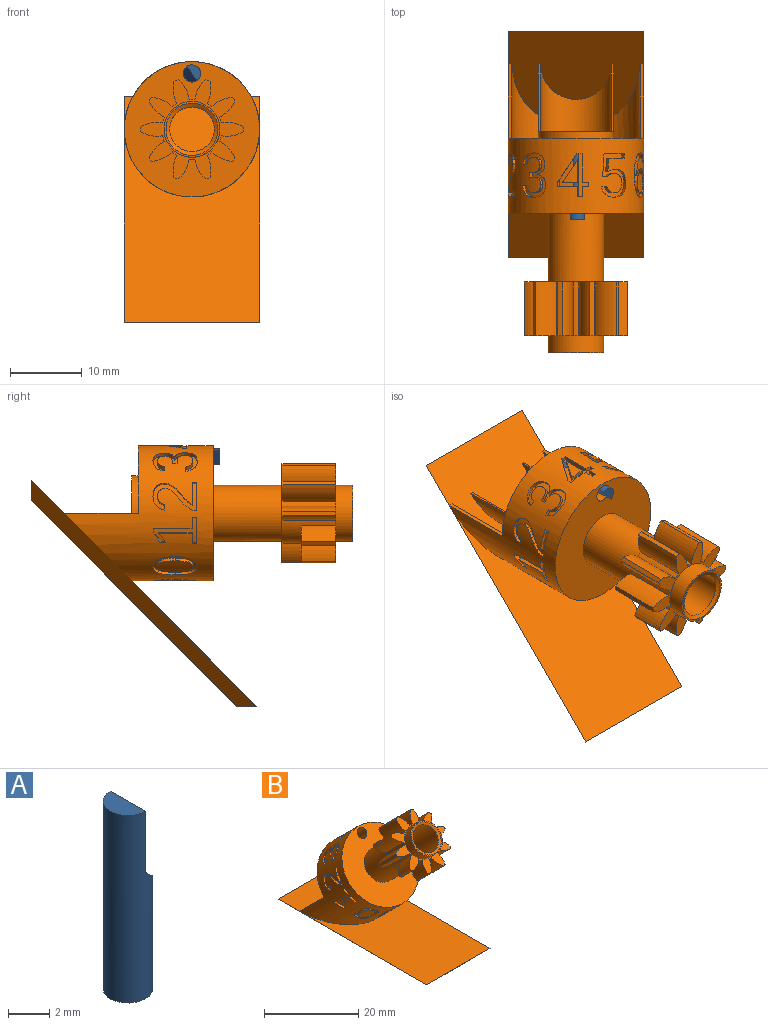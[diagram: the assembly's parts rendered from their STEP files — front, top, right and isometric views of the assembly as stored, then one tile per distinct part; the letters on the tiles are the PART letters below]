
ASSEMBLY  parts=2 mates=1
PART A: 5 faces, bbox 2.4x2.4x11.1 mm
  f0: cylinder r=1.2mm len=11.1mm, axis (0,0,-1), area 67.2mm2, adj f1,f2,f3,f4
  f1: plane 2.4x1.2mm, normal (0,0,1), area 2.3mm2, adj f0,f3
  f2: plane 2.4x2.4mm, normal (0,0,-1), area 4.5mm2, adj f0
  f3: plane 3.6x2.4mm, normal (1,0,0), area 8.6mm2, adj f0,f1,f4
  f4: plane 2.4x1.2mm, normal (0.71,0,0.71), area 3.2mm2, adj f0,f3
PART B: 299 faces, bbox 19.1x44.8x38.5 mm
  f0: cylinder r=9.45mm len=28.12mm, axis (0,0.71,-0.71), area 620.5mm2, adj f2,f4,f53,f54,f62,f63,f64,f65
  f1: cylinder r=5.25mm len=14.76mm, axis (0,0.71,-0.71), area 130.8mm2, adj f5,f6,f8,f53,f293
  f2: plane 7.34x7.34mm, normal (0,0.71,0.71), area 5.2mm2, adj f0,f3,f53,f293
  f3: cylinder r=8.95mm len=17.9mm, axis (0,-0.71,0.71), area 131.5mm2, adj f2,f4,f53,f293
  f4: plane 7.34x7.34mm, normal (0,0.71,0.71), area 5.2mm2, adj f0,f3,f53,f293
  f5: plane 6.7x6.7mm, normal (0,0.71,0.71), area 2.8mm2, adj f1,f7,f8,f293
  f6: plane 6.7x6.7mm, normal (0,0.71,0.71), area 2.8mm2, adj f1,f7,f8,f293
  f7: cylinder r=4.95mm len=10.2mm, axis (0,-0.71,0.71), area 98.3mm2, adj f5,f6,f8,f293
  f8: plane 10.5x7.21mm, normal (0,0.71,-0.71), area 26.4mm2, adj f1,f5,f6,f7,f52
  f9: plane 14.4x9.81mm, normal (0,0.71,-0.71), area 46.7mm2, adj f10,f11,f12,f19,f20,f21,f22,f23
  f10: cylinder r=4.5mm len=5.77mm, axis (0,0.71,-0.71), area 24.1mm2, adj f9,f11,f47,f48
  f11: cylinder r=7.2mm len=5.75mm, axis (0,0.71,-0.71), area 4.8mm2, adj f9,f10,f12,f48
  f12: cylinder r=4.5mm len=5.77mm, axis (0,0.71,-0.71), area 24.1mm2, adj f9,f11,f19,f48
  f13: cylinder r=4.5mm len=5.02mm, axis (0,0.71,-0.71), area 15.4mm2, adj f14,f19,f48,f50
  f14: cylinder r=7.2mm len=3.76mm, axis (0,0.71,-0.71), area 3.1mm2, adj f13,f15,f48,f50
  f15: cylinder r=4.5mm len=4.34mm, axis (0,0.71,-0.71), area 15.4mm2, adj f14,f19,f48,f50
  f16: cylinder r=4.5mm len=5.6mm, axis (0,0.71,-0.71), area 15.4mm2, adj f17,f19,f48,f49
  f17: cylinder r=7.2mm len=3.53mm, axis (0,0.71,-0.71), area 3.1mm2, adj f16,f18,f48,f49
  f18: cylinder r=4.5mm len=5.34mm, axis (0,0.71,-0.71), area 15.4mm2, adj f17,f19,f48,f49
  f19: cylinder r=4.2mm len=7.63mm, axis (0,0.71,-0.71), area 28mm2, adj f9,f12,f13,f15,f16,f18,f20,f48
  f20: cylinder r=4.5mm len=7.25mm, axis (0,0.71,-0.71), area 24.1mm2, adj f9,f19,f21,f48
  f21: cylinder r=7.2mm len=5.44mm, axis (0,0.71,-0.71), area 4.8mm2, adj f9,f20,f22,f48
  f22: cylinder r=4.5mm len=7.51mm, axis (0,0.71,-0.71), area 24.1mm2, adj f9,f21,f23,f48
  f23: cylinder r=4.2mm len=5.64mm, axis (0,0.71,-0.71), area 6mm2, adj f9,f22,f24,f48
  f24: cylinder r=4.5mm len=6.25mm, axis (0,0.71,-0.71), area 24.1mm2, adj f9,f23,f25,f48
  f25: cylinder r=7.2mm len=5.67mm, axis (0,0.71,-0.71), area 4.8mm2, adj f9,f24,f26,f48
  f26: cylinder r=4.5mm len=6.93mm, axis (0,0.71,-0.71), area 24.1mm2, adj f9,f25,f27,f48
  f27: cylinder r=4.2mm len=5.84mm, axis (0,0.71,-0.71), area 6mm2, adj f9,f26,f28,f48
  f28: cylinder r=4.5mm len=5.77mm, axis (0,0.71,-0.71), area 24.1mm2, adj f9,f27,f29,f48
  f29: cylinder r=7.2mm len=5.75mm, axis (0,0.71,-0.71), area 4.8mm2, adj f9,f28,f30,f48
  f30: cylinder r=4.5mm len=5.77mm, axis (0,0.71,-0.71), area 24.1mm2, adj f9,f29,f31,f48
  f31: cylinder r=4.2mm len=5.84mm, axis (0,0.71,-0.71), area 6mm2, adj f9,f30,f32,f48
  f32: cylinder r=4.5mm len=6.93mm, axis (0,0.71,-0.71), area 24.1mm2, adj f9,f31,f33,f48
  f33: cylinder r=7.2mm len=5.67mm, axis (0,0.71,-0.71), area 4.8mm2, adj f9,f32,f34,f48
  f34: cylinder r=4.5mm len=6.25mm, axis (0,0.71,-0.71), area 24.1mm2, adj f9,f33,f35,f48
  f35: cylinder r=4.2mm len=5.64mm, axis (0,0.71,-0.71), area 6mm2, adj f9,f34,f36,f48
  f36: cylinder r=4.5mm len=7.51mm, axis (0,0.71,-0.71), area 24.1mm2, adj f9,f35,f37,f48
  f37: cylinder r=7.2mm len=5.44mm, axis (0,0.71,-0.71), area 4.8mm2, adj f9,f36,f38,f48
  f38: cylinder r=4.5mm len=7.25mm, axis (0,0.71,-0.71), area 24.1mm2, adj f9,f37,f39,f48
  f39: cylinder r=4.2mm len=5.32mm, axis (0,0.71,-0.71), area 6mm2, adj f9,f38,f40,f48
  f40: cylinder r=4.5mm len=7.25mm, axis (0,0.71,-0.71), area 24.1mm2, adj f9,f39,f41,f48
  f41: cylinder r=7.2mm len=5.44mm, axis (0,0.71,-0.71), area 4.8mm2, adj f9,f40,f42,f48
  f42: cylinder r=4.5mm len=7.51mm, axis (0,0.71,-0.71), area 24.1mm2, adj f9,f41,f43,f48
  f43: cylinder r=4.2mm len=5.64mm, axis (0,0.71,-0.71), area 6mm2, adj f9,f42,f44,f48
  f44: cylinder r=4.5mm len=6.25mm, axis (0,0.71,-0.71), area 24.1mm2, adj f9,f43,f45,f48
  f45: cylinder r=7.2mm len=5.67mm, axis (0,0.71,-0.71), area 4.8mm2, adj f9,f44,f46,f48
  f46: cylinder r=4.5mm len=6.93mm, axis (0,0.71,-0.71), area 24.1mm2, adj f9,f45,f47,f48
  f47: cylinder r=4.2mm len=5.84mm, axis (0,0.71,-0.71), area 6mm2, adj f9,f10,f46,f48
  f48: plane 14.4x9.81mm, normal (0,-0.71,0.71), area 56.4mm2, adj f10,f11,f12,f13,f14,f15,f16,f17
  f49: plane 2.35x2.35mm, normal (0,0.71,-0.71), area 4.9mm2, adj f16,f17,f18,f19
  f50: plane 3.22x1.99mm, normal (0,0.71,-0.71), area 4.9mm2, adj f13,f14,f15,f19
  f51: cylinder r=3.9mm len=12.3mm, axis (0,0.71,-0.71), area 235.2mm2, adj f9,f54
  f52: cone r=3.12mm half-angle=30deg, axis (0,0.71,-0.71), area 49.7mm2, adj f8,f57
  f53: plane 18.9x13.01mm, normal (0,0.71,-0.71), area 175mm2, adj f0,f1,f2,f3,f4,f58
  f54: plane 18.9x13.36mm, normal (0,-0.71,0.71), area 228.2mm2, adj f0,f51,f58
  f55: cylinder r=3.9mm len=7.8mm, axis (0,0.71,-0.71), area 58.8mm2, adj f48,f56
  f56: plane 7.8x5.52mm, normal (0,-0.71,0.71), area 6.2mm2, adj f55,f59
  f57: cylinder r=3.12mm len=24.73mm, axis (0,0.71,-0.71), area 563.2mm2, adj f52,f59
  f58: cylinder r=1.2mm len=9.12mm, axis (0,-0.71,0.71), area 77.2mm2, adj f53,f54,f60,f61,f62,f63,f64,f65
  f59: cone r=3.64mm half-angle=60deg, axis (0,-0.71,0.71), area 12.7mm2, adj f56,f57
  f60: cylinder r=8.95mm len=4.38mm, axis (0,0.71,-0.71), area 4mm2, adj f58,f62,f66,f73,f74,f75,f76,f77
  f61: cylinder r=8.95mm len=2.98mm, axis (0,0.71,-0.71), area 3.2mm2, adj f58,f64,f65,f67,f71,f72,f79,f80
  f62: plane 0.74x0.39mm, normal (0,0.71,-0.71), area 0.4mm2, adj f0,f58,f60,f63,f75
  f63: plane 1.29x1.29mm, normal (1,0.02,0.02), area 0.6mm2, adj f0,f58,f62,f64
  f64: plane 2.84x0.57mm, normal (0,0.71,-0.71), area 1.4mm2, adj f0,f58,f61,f63,f72,f78
  f65: plane 3.46x2.95mm, normal (0.83,-0.38,0.41), area 2.4mm2, adj f0,f58,f61,f66,f72,f78
  f66: plane 0.82x0.39mm, normal (0,-0.71,0.71), area 0.4mm2, adj f0,f58,f60,f65,f76
  f67: plane 2.07x1.83mm, normal (-0.83,0.38,-0.41), area 1.4mm2, adj f58,f61,f68,f80,f138
  f68: extruded ~0.53x0.52mm, area 0.1mm2, adj f58,f67,f69,f138
  f69: extruded ~0.5x0.49mm, area 0.1mm2, adj f58,f68,f70,f138
  f70: plane 2.58x2.58mm, normal (1,0.02,0.02), area 1.5mm2, adj f58,f69,f71,f138
  f71: plane 2.13x0.5mm, normal (0,-0.71,0.71), area 1mm2, adj f58,f61,f70,f79,f138
  f72: plane 0.75x0.74mm, normal (-0.02,0.71,0.71), area 0.3mm2, adj f61,f64,f65,f78
  f73: plane 0.79x0.79mm, normal (-1,-0.02,-0.02), area 0.3mm2, adj f0,f60,f74,f77
  f74: plane 0.86x0.45mm, normal (0,0.71,-0.71), area 0.4mm2, adj f0,f60,f73,f75
  f75: plane 1.32x1.32mm, normal (-1,-0.02,-0.02), area 0.7mm2, adj f0,f60,f62,f74
  f76: plane 3.22x3.22mm, normal (-1,-0.02,-0.02), area 2mm2, adj f0,f60,f66,f77
  f77: plane 0.86x0.45mm, normal (0,-0.71,0.71), area 0.4mm2, adj f0,f60,f73,f76
  f78: plane 0.73x0.73mm, normal (1,0.02,0.02), area 0.3mm2, adj f0,f64,f65,f72
  f79: plane 0.43x0.41mm, normal (-0.78,0.43,-0.46), area 0.1mm2, adj f61,f71,f80,f138
  f80: plane 0.61x0.55mm, normal (-0.81,0.4,-0.43), area 0.2mm2, adj f61,f67,f79,f138
  f81: cylinder r=8.95mm len=6.17mm, axis (0,0.71,-0.71), area 9.9mm2, adj f82,f83,f84,f85,f86,f87,f88,f89
  f82: plane 0.31x0.29mm, normal (-0.78,-0.44,-0.44), area 0mm2, adj f0,f81,f83,f110
  f83: extruded ~1.11x1.09mm, area 0.5mm2, adj f0,f81,f82,f84
  f84: extruded ~1.12x0.84mm, area 0.5mm2, adj f0,f81,f83,f85
  f85: extruded ~1.38x0.94mm, area 0.7mm2, adj f0,f81,f84,f86
  f86: extruded ~1.47x1.24mm, area 0.8mm2, adj f0,f81,f85,f87
  f87: extruded ~1.45x1.23mm, area 0.7mm2, adj f0,f81,f86,f88
  f88: extruded ~1.43x0.9mm, area 0.7mm2, adj f0,f81,f87,f89,f112
  f89: plane 0.83x0.74mm, normal (0.06,0.74,-0.67), area 0.4mm2, adj f0,f81,f88,f90,f112
  f90: extruded ~0.99x0.66mm, area 0.4mm2, adj f0,f81,f89,f91
  f91: extruded ~0.99x0.85mm, area 0.4mm2, adj f0,f81,f90,f92
  f92: extruded ~0.99x0.86mm, area 0.5mm2, adj f0,f81,f91,f93
  f93: extruded ~0.96x0.71mm, area 0.4mm2, adj f0,f81,f92,f94
  f94: extruded ~0.99x0.68mm, area 0.4mm2, adj f0,f81,f93,f95
  f95: extruded ~1.09x0.91mm, area 0.5mm2, adj f0,f81,f94,f96
  f96: plane 0.62x0.48mm, normal (0,-0.71,0.71), area 0.2mm2, adj f0,f81,f95,f97
  f97: plane 0.75x0.75mm, normal (0.78,0.44,0.44), area 0.3mm2, adj f0,f81,f96,f98
  f98: plane 0.64x0.48mm, normal (0,0.71,-0.71), area 0.2mm2, adj f0,f81,f97,f99
  f99: extruded ~1.18x0.97mm, area 0.6mm2, adj f0,f81,f98,f100
  f100: extruded ~1.01x0.68mm, area 0.4mm2, adj f0,f81,f99,f101
  f101: extruded ~1.04x0.75mm, area 0.5mm2, adj f0,f81,f100,f102
  f102: extruded ~1.05x0.9mm, area 0.5mm2, adj f0,f81,f101,f103
  f103: extruded ~1.67x1.41mm, area 0.9mm2, adj f0,f81,f102,f104
  f104: plane 0.84x0.76mm, normal (0.07,-0.66,0.74), area 0.4mm2, adj f0,f81,f103,f105,f111
  f105: extruded ~1.49x0.92mm, area 0.7mm2, adj f0,f81,f104,f106,f111
  f106: extruded ~1.54x1.28mm, area 0.8mm2, adj f0,f81,f105,f107
  f107: extruded ~1.57x1.33mm, area 0.8mm2, adj f0,f81,f106,f108
  f108: extruded ~1.48x1.02mm, area 0.7mm2, adj f0,f81,f107,f109
  f109: extruded ~1.16x0.83mm, area 0.5mm2, adj f0,f81,f108,f110
  f110: extruded ~1.21x1.13mm, area 0.6mm2, adj f0,f81,f82,f109
  f111: plane 0.39x0.35mm, normal (-0.62,0.55,0.55), area 0mm2, adj f81,f104,f105
  f112: plane 0.04x0.04mm, normal (-0.62,0.55,0.55), area 0mm2, adj f81,f88,f89
  f113: cylinder r=8.95mm len=7.04mm, axis (0,0.71,-0.71), area 8.9mm2, adj f114,f115,f116,f117,f118,f119,f120,f121
  f114: plane 2.21x2.21mm, normal (0,-0.71,0.71), area 1.6mm2, adj f0,f113,f115,f137
  f115: extruded ~0.83x0.64mm, area 0.4mm2, adj f0,f113,f114,f116
  f116: extruded ~1.15x0.72mm, area 0.5mm2, adj f0,f113,f115,f117
  f117: extruded ~1.69x0.88mm, area 0.8mm2, adj f0,f113,f116,f118
  f118: extruded ~0.92x0.69mm, area 0.4mm2, adj f0,f113,f117,f119
  f119: extruded ~0.7x0.56mm, area 0.4mm2, adj f0,f113,f118,f120
  f120: extruded ~1.31x0.7mm, area 0.7mm2, adj f0,f113,f119,f121
  f121: extruded ~1.37x0.95mm, area 0.8mm2, adj f0,f113,f120,f122
  f122: extruded ~1.34x0.95mm, area 0.7mm2, adj f0,f113,f121,f123
  f123: extruded ~1.35x0.77mm, area 0.7mm2, adj f0,f113,f122,f124
  f124: plane 0.71x0.61mm, normal (0.02,0.77,-0.64), area 0.4mm2, adj f0,f113,f123,f125
  f125: extruded ~0.89x0.63mm, area 0.4mm2, adj f0,f113,f124,f126
  f126: extruded ~0.84x0.74mm, area 0.4mm2, adj f0,f113,f125,f127
  f127: extruded ~0.84x0.72mm, area 0.4mm2, adj f0,f113,f126,f128
  f128: extruded ~0.84x0.59mm, area 0.4mm2, adj f0,f113,f127,f129
  f129: extruded ~0.68x0.55mm, area 0.3mm2, adj f0,f113,f128,f130
  f130: extruded ~0.79x0.63mm, area 0.4mm2, adj f0,f113,f129,f131
  f131: extruded ~0.89x0.65mm, area 0.4mm2, adj f0,f113,f130,f132
  f132: extruded ~0.97x0.7mm, area 0.4mm2, adj f0,f113,f131,f133
  f133: extruded ~1.05x0.75mm, area 0.5mm2, adj f0,f113,f132,f134
  f134: extruded ~1.1x0.74mm, area 0.5mm2, adj f0,f113,f133,f135
  f135: plane 0.5x0.48mm, normal (0.26,0.68,0.68), area 0.3mm2, adj f0,f113,f134,f136
  f136: plane 2.82x2.82mm, normal (0,0.71,-0.71), area 2mm2, adj f0,f113,f135,f137
  f137: plane 0.56x0.56mm, normal (-0.26,-0.68,-0.68), area 0.3mm2, adj f0,f113,f114,f136
  f138: cylinder r=9.45mm len=2.39mm, axis (0,0.71,-0.71), area 3.3mm2, adj f67,f68,f69,f70,f71,f79,f80
  f139: cylinder r=8.95mm len=5.96mm, axis (0,0.71,-0.71), area 9.8mm2, adj f140,f141,f142,f143,f144,f145,f146,f147
  f140: extruded ~1.35x1.12mm, area 0.7mm2, adj f0,f139,f141,f160
  f141: plane 1.68x1.6mm, normal (-0.81,0.45,0.37), area 1mm2, adj f0,f139,f140,f142
  f142: plane 2.46x1.45mm, normal (0,0.71,-0.71), area 1.4mm2, adj f0,f139,f141,f143
  f143: plane 0.75x0.75mm, normal (-0.81,0.41,0.41), area 0.3mm2, adj f0,f139,f142,f144
  f144: plane 3.1x1.68mm, normal (0,-0.71,0.71), area 1.7mm2, adj f0,f139,f143,f145
  f145: plane 2.65x2.53mm, normal (0.81,-0.45,-0.37), area 1.7mm2, adj f0,f139,f144,f146
  f146: plane 0.99x0.52mm, normal (0,0.71,-0.71), area 0.4mm2, adj f0,f139,f145,f147
  f147: extruded ~0.78x0.77mm, area 0.3mm2, adj f0,f139,f146,f148
  f148: extruded ~0.78x0.61mm, area 0.3mm2, adj f0,f139,f147,f149
  f149: extruded ~1.08x0.95mm, area 0.5mm2, adj f0,f139,f148,f150
  f150: extruded ~1.11x0.82mm, area 0.5mm2, adj f0,f139,f149,f151
  f151: extruded ~1.18x0.89mm, area 0.6mm2, adj f0,f139,f150,f152
  f152: extruded ~1.1x0.97mm, area 0.5mm2, adj f0,f139,f151,f153
  f153: extruded ~1.5x1.37mm, area 0.8mm2, adj f0,f139,f152,f154
  f154: plane 1.01x0.59mm, normal (0.09,-0.75,0.65), area 0.4mm2, adj f0,f139,f153,f155,f161
  f155: extruded ~1.38x0.89mm, area 0.7mm2, adj f0,f139,f154,f156,f161
  f156: extruded ~1.47x1.18mm, area 0.7mm2, adj f0,f139,f155,f157
  f157: extruded ~1.63x1.38mm, area 0.9mm2, adj f0,f139,f156,f158
  f158: extruded ~1.64x1.18mm, area 0.8mm2, adj f0,f139,f157,f159
  f159: extruded ~1.53x1.09mm, area 0.8mm2, adj f0,f139,f158,f160
  f160: extruded ~1.51x1.3mm, area 0.8mm2, adj f0,f139,f140,f159
  f161: plane 0.29x0.26mm, normal (0.58,0.57,0.57), area 0mm2, adj f139,f154,f155
  f162: cylinder r=8.95mm len=7.09mm, axis (0,0.71,-0.71), area 10.3mm2, adj f163,f164,f165,f166,f167,f168,f169,f170
  f163: extruded ~1.39x0.99mm, area 0.7mm2, adj f0,f162,f164,f177
  f164: extruded ~1.45x0.79mm, area 0.8mm2, adj f0,f162,f163,f165
  f165: extruded ~1.54x0.85mm, area 0.8mm2, adj f0,f162,f164,f166
  f166: extruded ~1.48x1.02mm, area 0.8mm2, adj f0,f162,f165,f167
  f167: extruded ~1.72x1.08mm, area 0.9mm2, adj f0,f162,f166,f168
  f168: extruded ~2.05x1.33mm, area 1.2mm2, adj f0,f162,f167,f169
  f169: extruded ~2.21x1.46mm, area 1.3mm2, adj f0,f162,f168,f170
  f170: extruded ~1.8x1.09mm, area 0.9mm2, adj f0,f162,f169,f171
  f171: extruded ~2.17x1.17mm, area 1.2mm2, adj f0,f162,f170,f172
  f172: plane 0.72x0.6mm, normal (-0.05,0.82,-0.58), area 0.4mm2, adj f0,f162,f171,f173
  f173: extruded ~1.31x0.84mm, area 0.7mm2, adj f0,f162,f172,f174
  f174: extruded ~1.24x0.84mm, area 0.6mm2, adj f0,f162,f173,f175
  f175: extruded ~1.62x1.13mm, area 0.9mm2, adj f0,f162,f174,f176
  f176: extruded ~0.94x0.72mm, area 0.4mm2, adj f0,f162,f175,f177
  f177: extruded ~0.84x0.77mm, area 0.5mm2, adj f0,f162,f163,f176
  f178: extruded ~1.03x0.79mm, area 0.5mm2, adj f162,f179,f185,f289
  f179: extruded ~1.15x0.69mm, area 0.6mm2, adj f162,f178,f180,f289
  f180: extruded ~0.95x0.62mm, area 0.5mm2, adj f162,f179,f181,f289
  f181: extruded ~0.93x0.79mm, area 0.5mm2, adj f162,f180,f182,f289
  f182: extruded ~0.97x0.79mm, area 0.5mm2, adj f162,f181,f183,f289
  f183: extruded ~1.04x0.61mm, area 0.5mm2, adj f162,f182,f184,f289
  f184: extruded ~1.05x0.63mm, area 0.6mm2, adj f162,f183,f185,f289
  f185: extruded ~0.97x0.78mm, area 0.5mm2, adj f162,f178,f184,f289
  f186: cylinder r=8.95mm len=6.93mm, axis (0,0.71,-0.71), area 6.5mm2, adj f187,f188,f189,f190,f191,f192,f193,f194
  f187: plane 0.58x0.58mm, normal (-0.32,-0.67,-0.67), area 0.3mm2, adj f0,f186,f188,f196
  f188: plane 2.32x2.32mm, normal (0,0.71,-0.71), area 1.6mm2, adj f0,f186,f187,f189
  f189: extruded ~3.3x1.11mm, area 1.7mm2, adj f0,f186,f188,f190
  f190: extruded ~2.17x1.51mm, area 1.2mm2, adj f0,f186,f189,f191
  f191: plane 0.69x0.66mm, normal (0,0.71,-0.71), area 0.4mm2, adj f0,f186,f190,f192
  f192: extruded ~1.38x1.12mm, area 0.8mm2, adj f0,f186,f191,f193
  f193: extruded ~1.61x0.85mm, area 0.8mm2, adj f0,f186,f192,f194
  f194: extruded ~2.59x1.07mm, area 1.3mm2, adj f0,f186,f193,f195
  f195: plane 0.56x0.56mm, normal (0.32,0.67,0.67), area 0.3mm2, adj f0,f186,f194,f196
  f196: plane 2.79x2.79mm, normal (0,-0.71,0.71), area 2mm2, adj f0,f186,f187,f195
  f197: cylinder r=8.95mm len=6.04mm, axis (0,0.71,-0.71), area 11.8mm2, adj f198,f199,f200,f201,f202,f203,f204,f205
  f198: plane 0.73x0.73mm, normal (0.57,-0.58,-0.58), area 0mm2, adj f197,f204,f205
  f199: extruded ~1.09x1.07mm, area 0.5mm2, adj f0,f197,f200,f216
  f200: extruded ~1.16x0.9mm, area 0.5mm2, adj f0,f197,f199,f201
  f201: extruded ~1.48x1.06mm, area 0.7mm2, adj f0,f197,f200,f202
  f202: extruded ~1.6x1.3mm, area 0.8mm2, adj f0,f197,f201,f203
  f203: extruded ~1.61x1.31mm, area 0.8mm2, adj f0,f197,f202,f204
  f204: extruded ~1.49x1.05mm, area 0.8mm2, adj f0,f197,f198,f203,f205
  f205: extruded ~1.17x0.9mm, area 0.6mm2, adj f0,f197,f198,f204,f206
  f206: extruded ~1.07x1.06mm, area 0.5mm2, adj f0,f197,f205,f207
  f207: plane 0.3x0.3mm, normal (-0.82,-0.41,-0.41), area 0mm2, adj f0,f197,f206,f208
  f208: extruded ~1.03x0.99mm, area 0.5mm2, adj f0,f197,f207,f209
  f209: extruded ~1.08x0.85mm, area 0.5mm2, adj f0,f197,f208,f210
  f210: extruded ~1.35x0.93mm, area 0.6mm2, adj f0,f197,f209,f211
  f211: extruded ~1.49x1.23mm, area 0.7mm2, adj f0,f197,f210,f212
  f212: extruded ~1.49x1.21mm, area 0.8mm2, adj f0,f197,f211,f213
  f213: extruded ~1.35x0.94mm, area 0.7mm2, adj f0,f197,f212,f214
  f214: extruded ~1.08x0.85mm, area 0.5mm2, adj f0,f197,f213,f215
  f215: extruded ~1.01x0.98mm, area 0.5mm2, adj f0,f197,f214,f216
  f216: plane 0.3x0.3mm, normal (0.82,0.41,0.41), area 0mm2, adj f0,f197,f199,f215
  f217: extruded ~0.98x0.82mm, area 0.4mm2, adj f197,f218,f223,f231
  f218: extruded ~0.99x0.76mm, area 0.4mm2, adj f197,f217,f219,f231
  f219: extruded ~1.5x1.24mm, area 0.9mm2, adj f197,f218,f220,f231
  f220: extruded ~0.99x0.84mm, area 0.4mm2, adj f197,f219,f221,f231
  f221: extruded ~0.97x0.74mm, area 0.4mm2, adj f197,f220,f222,f231
  f222: extruded ~0.99x0.75mm, area 0.4mm2, adj f197,f221,f223,f231
  f223: extruded ~0.99x0.85mm, area 0.4mm2, adj f197,f217,f222,f231
  f224: extruded ~1.74x1.39mm, area 1mm2, adj f197,f225,f230,f290
  f225: extruded ~1.04x0.78mm, area 0.5mm2, adj f197,f224,f226,f290
  f226: extruded ~1.07x0.91mm, area 0.5mm2, adj f197,f225,f227,f290
  f227: extruded ~1.07x0.89mm, area 0.5mm2, adj f197,f226,f228,f290
  f228: extruded ~1.04x0.77mm, area 0.5mm2, adj f197,f227,f229,f290
  f229: extruded ~1.11x0.86mm, area 0.5mm2, adj f197,f228,f230,f290
  f230: extruded ~1.07x0.9mm, area 0.5mm2, adj f197,f224,f229,f290
  f231: cylinder r=9.45mm len=2.39mm, axis (0,0.71,-0.71), area 3.2mm2, adj f217,f218,f219,f220,f221,f222,f223
  f232: cylinder r=8.95mm len=4.57mm, axis (0,0.71,-0.71), area 10.5mm2, adj f233,f234,f235,f236,f237,f238,f239,f240
  f233: plane 0.48x0.48mm, normal (-0.03,-0.71,-0.71), area 0mm2, adj f232,f247,f248
  f234: extruded ~1.54x0.99mm, area 0.9mm2, adj f0,f232,f235,f249
  f235: extruded ~2.02x2mm, area 1.2mm2, adj f0,f232,f234,f236
  f236: extruded ~2.13x2.11mm, area 1.3mm2, adj f0,f232,f235,f237
  f237: extruded ~1.63x1.04mm, area 1mm2, adj f0,f232,f236,f238
  f238: extruded ~1.15x0.66mm, area 0.6mm2, adj f0,f232,f237,f239
  f239: extruded ~1.13x1.11mm, area 0.6mm2, adj f0,f232,f238,f240
  f240: plane 0.75x0.52mm, normal (-0.16,-0.7,0.7), area 0.4mm2, adj f0,f232,f239,f241
  f241: extruded ~1.03x0.97mm, area 0.7mm2, adj f0,f232,f240,f242
  f242: extruded ~1.04x0.83mm, area 0.6mm2, adj f0,f232,f241,f243
  f243: extruded ~1.63x1.62mm, area 0.9mm2, adj f0,f232,f242,f244
  f244: extruded ~0.84x0.82mm, area 0.4mm2, adj f0,f232,f243,f245
  f245: extruded ~0.92x0.54mm, area 0.5mm2, adj f0,f232,f244,f246
  f246: extruded ~1.31x0.87mm, area 0.7mm2, adj f0,f232,f245,f247
  f247: extruded ~1.48x1.46mm, area 0.8mm2, adj f0,f232,f233,f246,f248
  f248: extruded ~1.49x1.47mm, area 0.8mm2, adj f0,f232,f233,f247,f249
  f249: extruded ~1.49x0.86mm, area 0.8mm2, adj f0,f232,f234,f248
  f250: extruded ~0.63x0.48mm, area 0.3mm2, adj f232,f251,f258,f291
  f251: extruded ~0.88x0.68mm, area 0.5mm2, adj f232,f250,f252,f291
  f252: extruded ~1.13x1.12mm, area 0.6mm2, adj f232,f251,f253,f291
  f253: extruded ~1.11x1.1mm, area 0.6mm2, adj f232,f252,f254,f291
  f254: extruded ~0.89x0.68mm, area 0.5mm2, adj f232,f253,f255,f291
  f255: extruded ~0.91x0.7mm, area 0.5mm2, adj f232,f254,f256,f291
  f256: extruded ~1.21x1.2mm, area 0.6mm2, adj f232,f255,f257,f291
  f257: extruded ~0.82x0.81mm, area 0.3mm2, adj f232,f256,f258,f291
  f258: extruded ~0.69x0.67mm, area 0.3mm2, adj f232,f250,f257,f291
  f259: cylinder r=8.95mm len=6.13mm, axis (0,0.71,-0.71), area 9.9mm2, adj f260,f261,f262,f263,f264,f265,f266,f267
  f260: plane 1.9x1.9mm, normal (-0.62,-0.56,-0.56), area 0.2mm2, adj f259,f266,f267
  f261: extruded ~1.62x1.58mm, area 0.9mm2, adj f0,f259,f262,f268
  f262: extruded ~2.19x1.75mm, area 1.2mm2, adj f0,f259,f261,f263
  f263: extruded ~2.2x1.73mm, area 1.2mm2, adj f0,f259,f262,f264
  f264: extruded ~1.61x1.59mm, area 0.9mm2, adj f0,f259,f263,f265
  f265: extruded ~1.63x1.61mm, area 0.9mm2, adj f0,f259,f264,f266
  f266: extruded ~2.19x1.73mm, area 1.2mm2, adj f0,f259,f260,f265,f267
  f267: extruded ~2.19x1.75mm, area 1.2mm2, adj f0,f259,f260,f266,f268
  f268: extruded ~1.67x1.62mm, area 0.9mm2, adj f0,f259,f261,f267
  f269: extruded ~1.17x1.14mm, area 0.6mm2, adj f259,f270,f276,f292
  f270: extruded ~1.77x1.49mm, area 1mm2, adj f259,f269,f271,f292
  f271: extruded ~1.78x1.51mm, area 1mm2, adj f259,f270,f272,f292
  f272: extruded ~1.17x1.15mm, area 0.6mm2, adj f259,f271,f273,f292
  f273: extruded ~1.15x1.12mm, area 0.6mm2, adj f259,f272,f274,f292
  f274: extruded ~1.77x1.5mm, area 1mm2, adj f259,f273,f275,f292
  f275: extruded ~1.75x1.48mm, area 1mm2, adj f259,f274,f276,f292
  f276: extruded ~1.16x1.12mm, area 0.6mm2, adj f259,f269,f275,f292
  f277: cylinder r=8.95mm len=6.83mm, axis (0,0.71,-0.71), area 7.6mm2, adj f278,f279,f280,f281,f282,f283,f284,f285
  f278: plane 1.13x1.13mm, normal (0,-0.71,0.71), area 0.7mm2, adj f0,f277,f279,f288
  f279: plane 3.89x3.89mm, normal (0.26,-0.68,-0.68), area 2.7mm2, adj f0,f277,f278,f280
  f280: plane 0.66x0.58mm, normal (0,-0.71,0.71), area 0.4mm2, adj f0,f277,f279,f281
  f281: plane 1.73x1.01mm, normal (-0.15,-0.2,0.97), area 0.9mm2, adj f0,f277,f280,f282
  f282: plane 0.61x0.61mm, normal (-0.26,0.68,0.68), area 0.4mm2, adj f0,f277,f281,f283
  f283: plane 1.68x0.99mm, normal (0.15,0.18,-0.97), area 0.8mm2, adj f0,f277,f282,f284
  f284: plane 3.37x3.37mm, normal (-0.26,0.68,0.68), area 2.3mm2, adj f0,f277,f283,f285
  f285: plane 1.11x1.11mm, normal (0,-0.71,0.71), area 0.8mm2, adj f0,f277,f284,f286
  f286: plane 0.56x0.56mm, normal (-0.26,0.68,0.68), area 0.3mm2, adj f0,f277,f285,f287
  f287: plane 2.67x2.67mm, normal (0,0.71,-0.71), area 1.9mm2, adj f0,f277,f286,f288
  f288: plane 0.56x0.56mm, normal (0.26,-0.68,-0.68), area 0.3mm2, adj f0,f277,f278,f287
  f289: cylinder r=9.45mm len=3.58mm, axis (0,0.71,-0.71), area 4.9mm2, adj f178,f179,f180,f181,f182,f183,f184,f185
  f290: cylinder r=9.45mm len=2.72mm, axis (0,0.71,-0.71), area 4.1mm2, adj f224,f225,f226,f227,f228,f229,f230
  f291: cylinder r=9.45mm len=2.42mm, axis (0,0.71,-0.71), area 5mm2, adj f250,f251,f252,f253,f254,f255,f256,f257
  f292: cylinder r=9.45mm len=4.62mm, axis (0,0.71,-0.71), area 9.9mm2, adj f269,f270,f271,f272,f273,f274,f275,f276
  f293: plane 44.61x19mm, normal (0,0,1), area 820.3mm2, adj f0,f1,f2,f3,f4,f5,f6,f7
  f294: plane 40.61x15mm, normal (0,0,-1), area 609.1mm2, adj f295,f296,f297,f298
  f295: plane 19x2mm, normal (0,-0.71,-0.71), area 48.1mm2, adj f293,f294,f296,f297
  f296: plane 44.61x2mm, normal (0.71,0,-0.71), area 120.5mm2, adj f293,f294,f295,f298
  f297: plane 44.61x2mm, normal (-0.71,0,-0.71), area 120.5mm2, adj f293,f294,f295,f298
  f298: plane 19x2mm, normal (0,0.71,-0.71), area 48.1mm2, adj f293,f294,f296,f297
PLACE A rot(axis=(0.22,0.69,-0.69),154.8deg) t=(0,-6.4,0.2)mm
PLACE B rot(axis=(1,0,0),45deg) t=(0,-5.2,-7.6)mm
MATE fastened A.f0 <-> B.f58  axis (0,1,0) through (0,-17.5,0.2)mm
